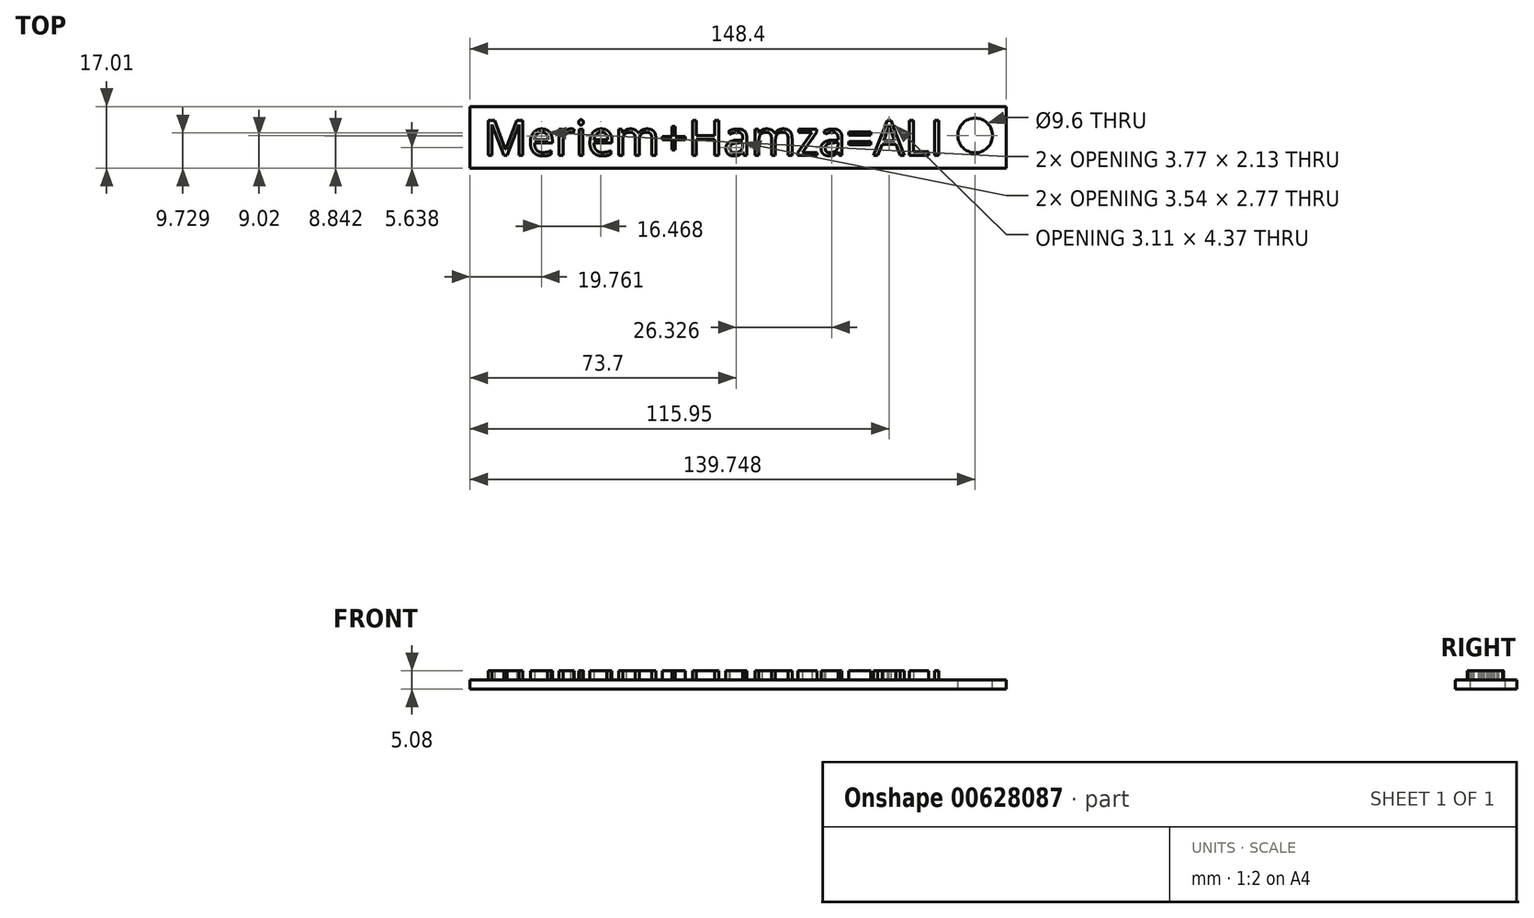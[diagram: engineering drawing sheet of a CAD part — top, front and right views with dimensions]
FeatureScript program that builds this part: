
annotation { "Feature Type Name" : "Feature", "Feature Type Description" : "" }
export const myFeature = defineFeature(function(context is Context, id is Id, definition is map)
    precondition{}
    {
        {
            var Q0;
            Q0=qCreatedBy(makeId("Top.planeOp"),FACE);
            var sketch = newSketch(context, id + "F0", { "sketchPlane" : qUnion([Q0])});
            skText(sketch, "E0", { "text": "Meriem+Hamza=ALI", "fontName": "OpenSans-Regular.ttf"});
            const initialGuessF0  = {"E0": [-0.00228, -0.00554, 1, 0, 0.0097]};
            skSetInitialGuess(sketch, initialGuessF0);
            skSolve(sketch);
        }
        {
            var Q0;
            Q0=qCreatedBy(makeId("Top.planeOp"),FACE);
            var sketch = newSketch(context, id + "F1", { "sketchPlane" : qUnion([Q0])});
            skLineSegment(sketch, "E1.bottom", {"start": v(-6.08, 8) * mm, "end": v(142.32, 8) * mm});
            skLineSegment(sketch, "E1.top", {"start": v(-6.08, -9.02) * mm, "end": v(142.32, -9.02) * mm});
            skLineSegment(sketch, "E1.left", {"start": v(-6.08, 8) * mm, "end": v(-6.08, -9.02) * mm});
            skLineSegment(sketch, "E1.right", {"start": v(142.32, 8) * mm, "end": v(142.32, -9.02) * mm});
            skCircle(sketch, "E2", {"center": v(133.67, 0) * mm, "radius": 4.8 * mm});
            skSolve(sketch);
        }
        {
            var Q0;
            Q0 = qSketchRegion(id + "F0", true);
            extrude(context, id + "F2", {"entities" : qUnion([Q0]), "depth" : 2.54 * mm, "offsetDistance" : 25.4 * mm});
        }
        {
            var Q0;
            Q0 = qSketchRegion(id + "F1", true);
            extrude(context, id + "F3", {"entities" : qUnion([Q0]), "oppositeDirection" : true, "depth" : 2.54 * mm, "offsetDistance" : 25.4 * mm});
        }
    });
